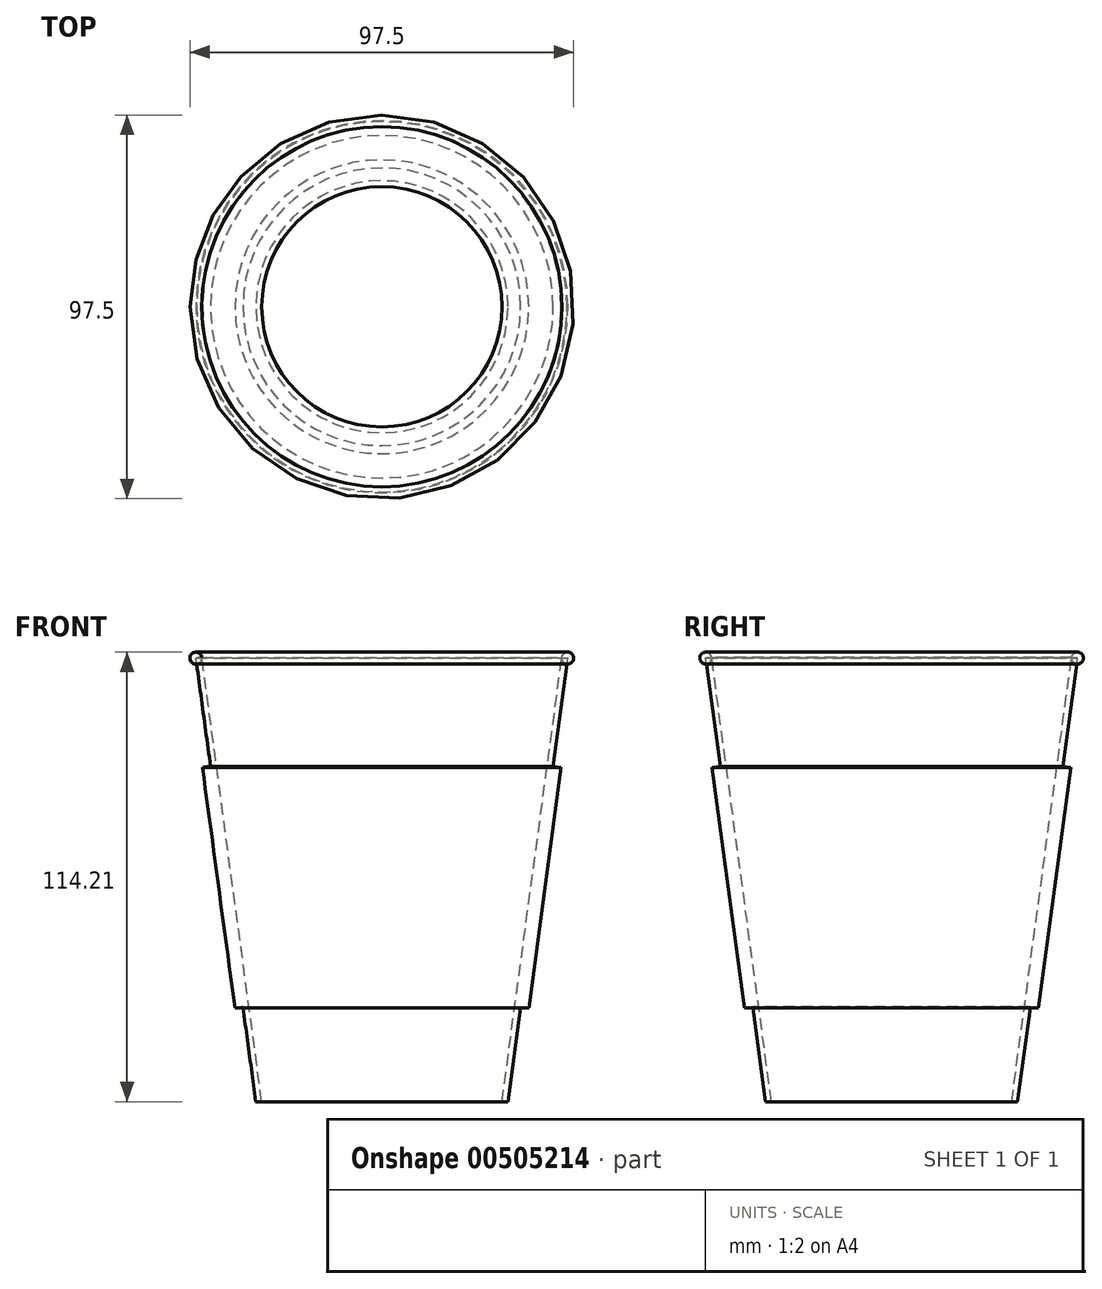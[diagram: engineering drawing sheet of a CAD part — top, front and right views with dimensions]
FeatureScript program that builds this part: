
annotation { "Feature Type Name" : "Feature", "Feature Type Description" : "" }
export const myFeature = defineFeature(function(context is Context, id is Id, definition is map)
    precondition{}
    {
        {
            var Q0;
            Q0=qCreatedBy(makeId("Front.planeOp"),FACE);
            var sketch = newSketch(context, id + "F0", { "sketchPlane" : qUnion([Q0])});
            skLineSegment(sketch, "E0", {"start": v(47.24, 57.73) * mm, "end": v(32.03, -54.98) * mm});
            skLineSegment(sketch, "E1", {"start": v(0, -54.98) * mm, "end": v(0, 54.98) * mm});
            skLineSegment(sketch, "E2", {"start": v(0, -54.98) * mm, "end": v(32.03, -54.98) * mm});
            skCircle(sketch, "E3", {"center": v(47.24, 57.73) * mm, "radius": 1.5 * mm});
            skLineSegment(sketch, "E4", {"start": v(47.24, 57.73) * mm, "end": v(45.75, 57.93) * mm});
            skLineSegment(sketch, "E5", {"start": v(45.75, 57.93) * mm, "end": v(30.5, -54.98) * mm});
            skLineSegment(sketch, "E6", {"start": v(43.53, 30.22) * mm, "end": v(45.57, 29.95) * mm});
            skLineSegment(sketch, "E7", {"start": v(45.57, 29.95) * mm, "end": v(37.33, -31.16) * mm});
            skLineSegment(sketch, "E8", {"start": v(37.33, -31.16) * mm, "end": v(35.28, -30.88) * mm});
            skSolve(sketch);
        }
        {
            var Q0;
            {var subQ0=sQuery(id+"F0.wireOp",EDGE,"E0");Q0=makeQuery(id+"F0.imprint","IMPRINT",FACE,{"disambiguationData":[TD([[makeQuery(id+"F0.imprint","IMPRINT",EDGE,{"derivedFrom":subQ0}),1.0]])]});}
            var Q1;
            {var subQ5=sQuery(id+"F0.wireOp",EDGE,"E5");Q1=makeQuery(id+"F0.imprint","IMPRINT",FACE,{"disambiguationData":[TD([[makeQuery(id+"F0.imprint","IMPRINT",EDGE,{"derivedFrom":subQ5}),1.0]])]});}
            var Q2;
            {var subQ0=sQuery(id+"F0.wireOp",EDGE,"E6");Q2=makeQuery(id+"F0.imprint","IMPRINT",FACE,{"disambiguationData":[TD([[makeQuery(id+"F0.imprint","IMPRINT",EDGE,{"derivedFrom":subQ0}),-1.0]])]});}
            var Q3;
            Q3=sQuery(id+"F0.wireOp",EDGE,"E1");
            revolve(context, id + "F1", {"entities" : qUnion([Q0, Q1, Q2]), "axis" : qUnion([Q3]), "revolveType" : RevolveType.FULL});
        }
    });
